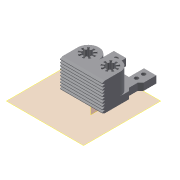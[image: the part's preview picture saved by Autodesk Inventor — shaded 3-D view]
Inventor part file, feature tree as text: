
AUTODESK INVENTOR PART (.ipt)
format: ipt  version: 2019.4 (Build 234330000, 330)  size: 493,056 bytes
history: native  units: mm
features: other x7, reference x6, extrude x5, sketch x5, plane x3, projected_geometry x2, pattern_linear x1, hole x1, fillet x1, pattern_circular x1, mirror x1
ambient origin geometry x8: Origin, YZ Plane, XZ Plane, XY Plane, X Axis, Y Axis, Z Axis, Center Point
bodies: Body1 (feature_tree)
feature tree (33):
  plane  "Work Plane8"
  extrude  "Extrusion11"  Depth=5.0mm TaperAngle=0.0deg
  plane  "Work Plane10"
  extrude  "Extrusion22"  Depth=10.0mm TaperAngle=0.0deg
  pattern_linear  "Rectangular Pattern3"  Count1=10 Spacing1=2.0mm
  hole  "Hole2"  [1 undecoded]
  extrude  "Extrusion24"  Depth=0.5mm
  extrude  "Extrusion25"  Depth=10.0mm TaperAngle=0.0deg
  fillet  "Fillet2"  Radius=2.0mm
  pattern_circular  "Circular Pattern1"  [2 undecoded]
  mirror  "Mirror4"
  extrude  "Extrusion26"  Depth=0.5mm
  sketch  "Sketch12"  dims[d64=180.0deg d66=5.0mm d67=0.0mm]
  reference  "Reference31"
  reference  "Reference32"
  reference  "Reference33"
  reference  "Reference35"
  reference  "Reference36"
  reference  "Reference42"
  sketch  "Sketch26"  dims[d1=0.4mm d114=10.0mm d115=0.0mm]
  sketch  "Sketch27"  dims[d125=0.2mm]
  projected_geometry  "Projected Loop13"
  sketch  "Sketch28"  dims[d126=0.0mm d128=100.0mm d130=2.0mm]
  plane  "Work Plane11"
  sketch  "Sketch29"  dims[d131=2.0mm d133=0.8mm d134=4.0mm d135=2.8mm d136=6.0mm d137=3.5mm d138=26.0mm d139=90.0deg d140=8.0mm d141=20.594885mm d142=10.0mm d143=0.0mm d144=2.0mm d145=10.0mm d146=0.0mm d147=0.5mm d148=90.0mm d149=360.0deg d151=45.0deg d152=135.0deg d153=1.0mm d154=1.0mm d155=0.0mm d156=0.0mm]
  projected_geometry  "Projected Loop14"
  other  "Assembly_Cube_Z_Focus_Drylin_NEMA_v3.iam"
  other  "00_Igus_Drylin_6mm:1"
  other  "00_Igus_Drylin_6mm:4"
  other  "30_Cube_Z_Focus_MGN_NEMA_adapter:1"
  other  "30_Cube_Z_Focus_Drylin_NEMA_base_v3:1"
  other  "Assembly_Cube_Z_Focus_Drylin_NEMA_slide.iam"
  other  "30_Cube_Z_Focus_Drylin_NEMA_slide_part1:1"
note: 3 required parameter values undecoded (feature->parameter linkage not recoverable at this tier; creation-order binding heuristic only, values carry confidence <= 0.55)
